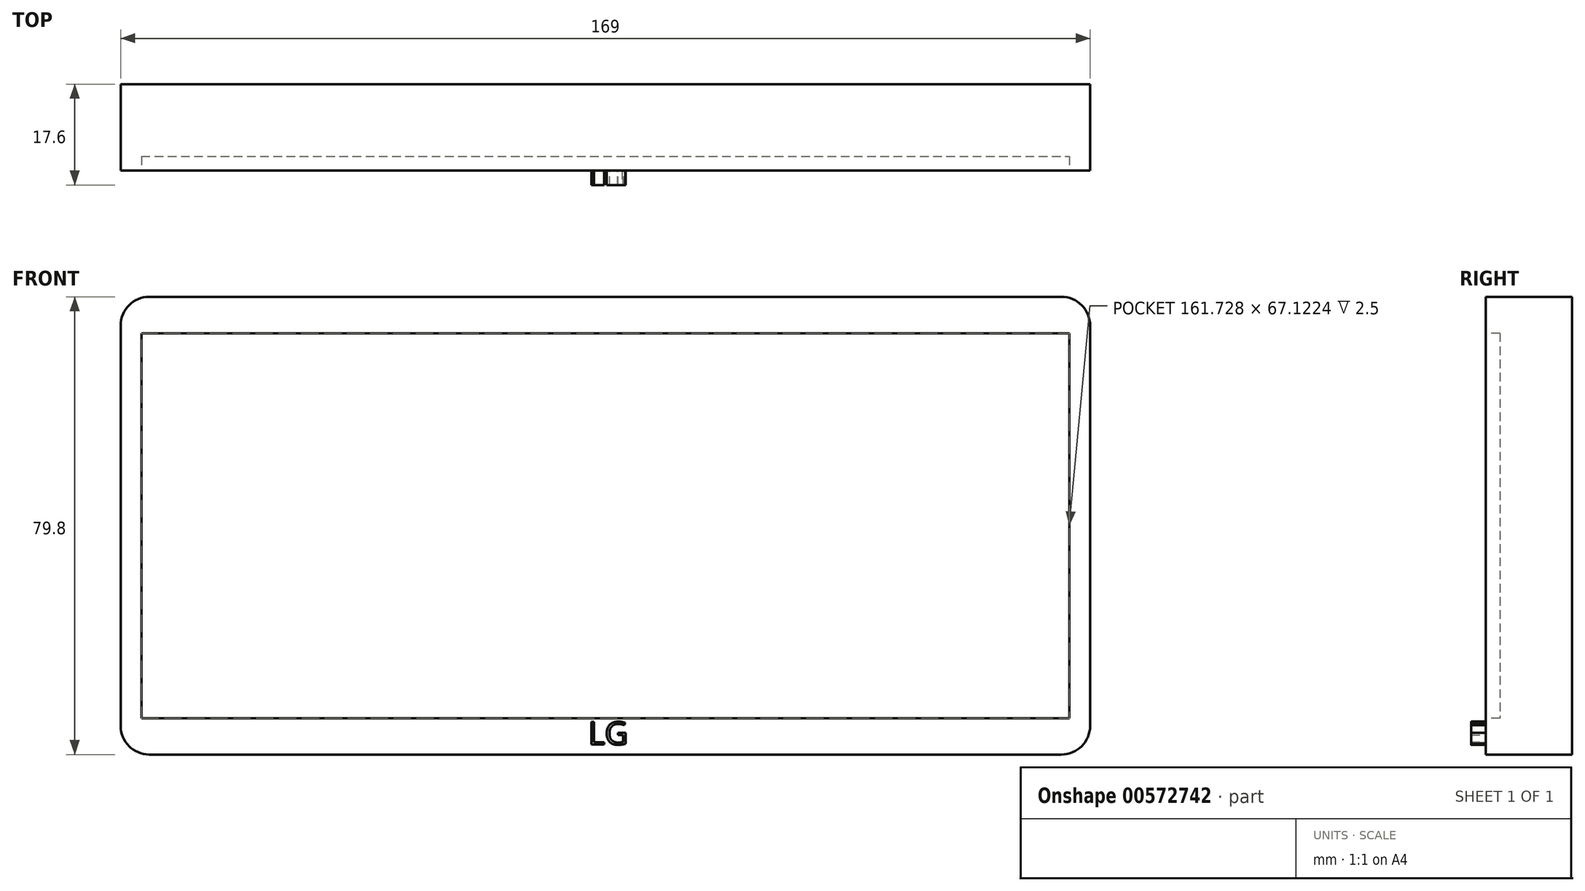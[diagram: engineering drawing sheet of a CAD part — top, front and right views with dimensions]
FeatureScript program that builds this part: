
annotation { "Feature Type Name" : "Feature", "Feature Type Description" : "" }
export const myFeature = defineFeature(function(context is Context, id is Id, definition is map)
    precondition{}
    {
        {
            var Q0;
            Q0=qCreatedBy(makeId("Front.planeOp"),FACE);
            var sketch = newSketch(context, id + "F0", { "sketchPlane" : qUnion([Q0])});
            skLineSegment(sketch, "E0.bottom", {"start": v(-84.5, 39.9) * mm, "end": v(84.5, 39.9) * mm});
            skLineSegment(sketch, "E0.top", {"start": v(-84.5, -39.9) * mm, "end": v(84.5, -39.9) * mm});
            skLineSegment(sketch, "E0.left", {"start": v(-84.5, 39.9) * mm, "end": v(-84.5, -39.9) * mm});
            skLineSegment(sketch, "E0.right", {"start": v(84.5, 39.9) * mm, "end": v(84.5, -39.9) * mm});
            skPoint(sketch, "E0.middle", {"position": v(0, 0) * mm});
            skSolve(sketch);
        }
        {
            var Q0;
            Q0=makeQuery(id+"F0.imprint","IMPRINT",FACE,{"disambiguationData":[TD([[makeQuery(id+"F0.imprint","IMPRINT",EDGE,{"derivedFrom":sQuery(id+"F0.wireOp",EDGE,"E0.bottom")}),-1.0]])]});
            extrude(context, id + "F1", {"entities" : qUnion([Q0]), "depth" : 15.1 * mm, "offsetDistance" : 25 * mm});
        }
        {
            var Q0;
            Q0=makeQuery(id+"F1.opExtrude","CAP_FACE",FACE,{"disambiguationData":[OSD([sQuery(id+"F0.wireOp",EDGE,"E0.bottom"),sQuery(id+"F0.wireOp",EDGE,"E0.top"),sQuery(id+"F0.wireOp",EDGE,"E0.left"),sQuery(id+"F0.wireOp",EDGE,"E0.right")])],"isStart":false});
            var sketch = newSketch(context, id + "F2", { "sketchPlane" : qUnion([Q0])});
            skLineSegment(sketch, "E1.bottom", {"start": v(-80.86, 33.56) * mm, "end": v(80.86, 33.56) * mm});
            skLineSegment(sketch, "E1.top", {"start": v(-80.86, -33.56) * mm, "end": v(80.86, -33.56) * mm});
            skLineSegment(sketch, "E1.left", {"start": v(-80.86, 33.56) * mm, "end": v(-80.86, -33.56) * mm});
            skLineSegment(sketch, "E1.right", {"start": v(80.86, 33.56) * mm, "end": v(80.86, -33.56) * mm});
            skPoint(sketch, "E1.middle", {"position": v(0, 0) * mm});
            skSolve(sketch);
        }
        {
            var Q0;
            Q0=makeQuery(id+"F2.imprint","IMPRINT",FACE,{"disambiguationData":[TD([[makeQuery(id+"F2.imprint","IMPRINT",EDGE,{"derivedFrom":sQuery(id+"F2.wireOp",EDGE,"E1.bottom")}),-1.0]])]});
            extrude(context, id + "F3", {"entities" : qUnion([Q0]), "operationType" : NewBodyOperationType.REMOVE, "oppositeDirection" : true, "depth" : 2.5 * mm, "offsetDistance" : 25 * mm});
        }
        {
            var Q0;
            Q0=makeQuery(id+"F1.opExtrude","CAP_FACE",FACE,{"disambiguationData":[OSD([sQuery(id+"F0.wireOp",EDGE,"E0.bottom"),sQuery(id+"F0.wireOp",EDGE,"E0.top"),sQuery(id+"F0.wireOp",EDGE,"E0.left"),sQuery(id+"F0.wireOp",EDGE,"E0.right")])],"isStart":false});
            var sketch = newSketch(context, id + "F4", { "sketchPlane" : qUnion([Q0])});
            skText(sketch, "E2", { "text": "LG", "fontName": "OpenSans-Regular.ttf"});
            const initialGuessF4  = {"E2": [-0.00298, -0.03817, 1, 0, 0.00399]};
            skSetInitialGuess(sketch, initialGuessF4);
            skSolve(sketch);
        }
        {
            var Q0;
            Q0=makeQuery(id+"F4.imprint","IMPRINT",FACE,{"disambiguationData":[TD([[makeQuery(id+"F4.imprint","IMPRINT",EDGE,{"derivedFrom":sQuery(id+"F4.wireOp",EDGE,"E2.sketch_text.stroke-0")}),-1.0]])]});
            var Q1;
            Q1=makeQuery(id+"F4.imprint","IMPRINT",FACE,{"disambiguationData":[TD([[makeQuery(id+"F4.imprint","IMPRINT",EDGE,{"derivedFrom":sQuery(id+"F4.wireOp",EDGE,"E2.sketch_text.stroke-6")}),-1.0]])]});
            extrude(context, id + "F5", {"entities" : qUnion([Q0, Q1]), "operationType" : NewBodyOperationType.ADD, "depth" : 2.5 * mm, "offsetDistance" : 25 * mm});
        }
        {
            var Q0;
            Q0=makeQuery(id+"F1.opExtrude","SWEPT_EDGE",EDGE,{"disambiguationData":[OSD([sQuery(id+"F0.wireOp",EDGE,"E0.bottom"),sQuery(id+"F0.wireOp",EDGE,"E0.left")])]});
            var Q1;
            Q1=makeQuery(id+"F1.opExtrude","SWEPT_EDGE",EDGE,{"disambiguationData":[OSD([sQuery(id+"F0.wireOp",EDGE,"E0.top"),sQuery(id+"F0.wireOp",EDGE,"E0.left")])]});
            var Q2;
            Q2=makeQuery(id+"F1.opExtrude","SWEPT_EDGE",EDGE,{"disambiguationData":[OSD([sQuery(id+"F0.wireOp",EDGE,"E0.bottom"),sQuery(id+"F0.wireOp",EDGE,"E0.right")])]});
            var Q3;
            Q3=makeQuery(id+"F1.opExtrude","SWEPT_EDGE",EDGE,{"disambiguationData":[OSD([sQuery(id+"F0.wireOp",EDGE,"E0.top"),sQuery(id+"F0.wireOp",EDGE,"E0.right")])]});
            fillet(context, id + "F6", {"entities" : qUnion([Q0, Q1, Q2, Q3]), "radius" : 5 * mm, "tangentPropagation" : true, "allowEdgeOverflow" : false});
        }
    });
